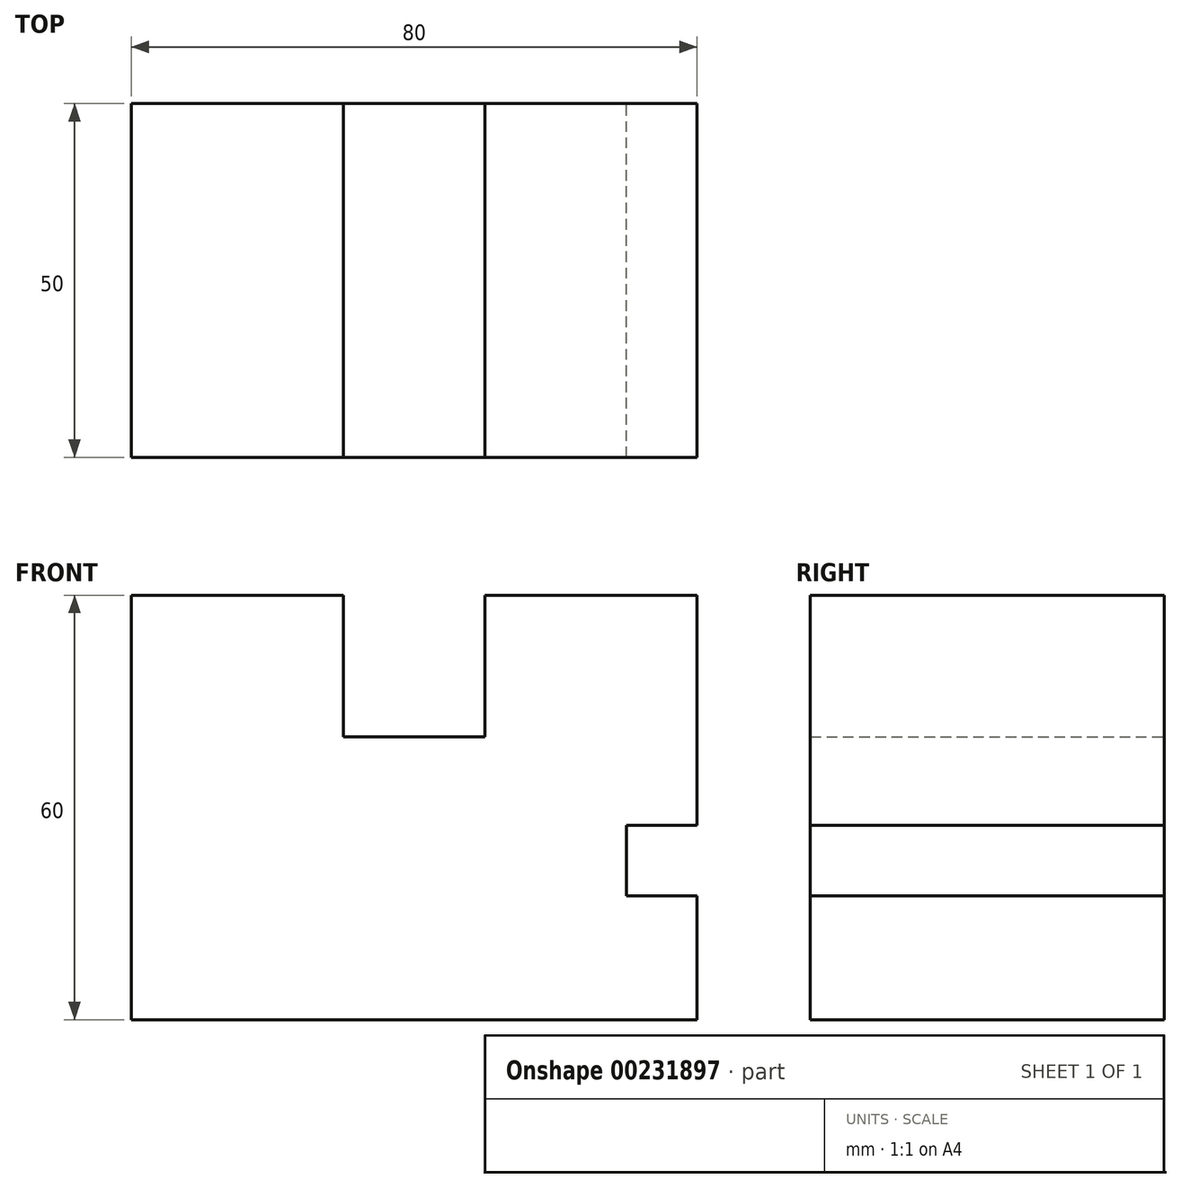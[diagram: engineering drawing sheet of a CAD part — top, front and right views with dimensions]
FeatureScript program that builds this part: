
annotation { "Feature Type Name" : "Feature", "Feature Type Description" : "" }
export const myFeature = defineFeature(function(context is Context, id is Id, definition is map)
    precondition{}
    {
        {
            var Q0;
            Q0=qCreatedBy(makeId("Front.planeOp"),FACE);
            var sketch = newSketch(context, id + "F0", { "sketchPlane" : qUnion([Q0])});
            skLineSegment(sketch, "E0", {"start": v(0, 0) * mm, "end": v(0, 60) * mm});
            skLineSegment(sketch, "E1", {"start": v(0, 60) * mm, "end": v(30, 60) * mm});
            skLineSegment(sketch, "E2", {"start": v(30, 60) * mm, "end": v(30, 40) * mm});
            skLineSegment(sketch, "E3", {"start": v(30, 40) * mm, "end": v(50, 40) * mm});
            skLineSegment(sketch, "E4", {"start": v(50, 40) * mm, "end": v(50, 60) * mm});
            skLineSegment(sketch, "E5", {"start": v(50, 60) * mm, "end": v(80, 60) * mm});
            skLineSegment(sketch, "E6", {"start": v(80, 60) * mm, "end": v(80, 27.47) * mm});
            skLineSegment(sketch, "E7", {"start": v(80, 27.47) * mm, "end": v(70, 27.47) * mm});
            skLineSegment(sketch, "E8", {"start": v(70, 27.47) * mm, "end": v(70, 17.47) * mm});
            skLineSegment(sketch, "E9", {"start": v(70, 17.47) * mm, "end": v(80, 17.47) * mm});
            skLineSegment(sketch, "E10", {"start": v(80, 17.47) * mm, "end": v(80, 0) * mm});
            skLineSegment(sketch, "E11", {"start": v(80, 0) * mm, "end": v(0, 0) * mm});
            skSolve(sketch);
        }
        {
            var Q0;
            Q0=makeQuery(id+"F0.imprint","IMPRINT",FACE,{"disambiguationData":[TD([[makeQuery(id+"F0.imprint","IMPRINT",EDGE,{"derivedFrom":sQuery(id+"F0.wireOp",EDGE,"E0")}),-1.0]])]});
            extrude(context, id + "F1", {"entities" : qUnion([Q0]), "endBound" : BoundingType.SYMMETRIC, "depth" : 50 * mm});
        }
    });
